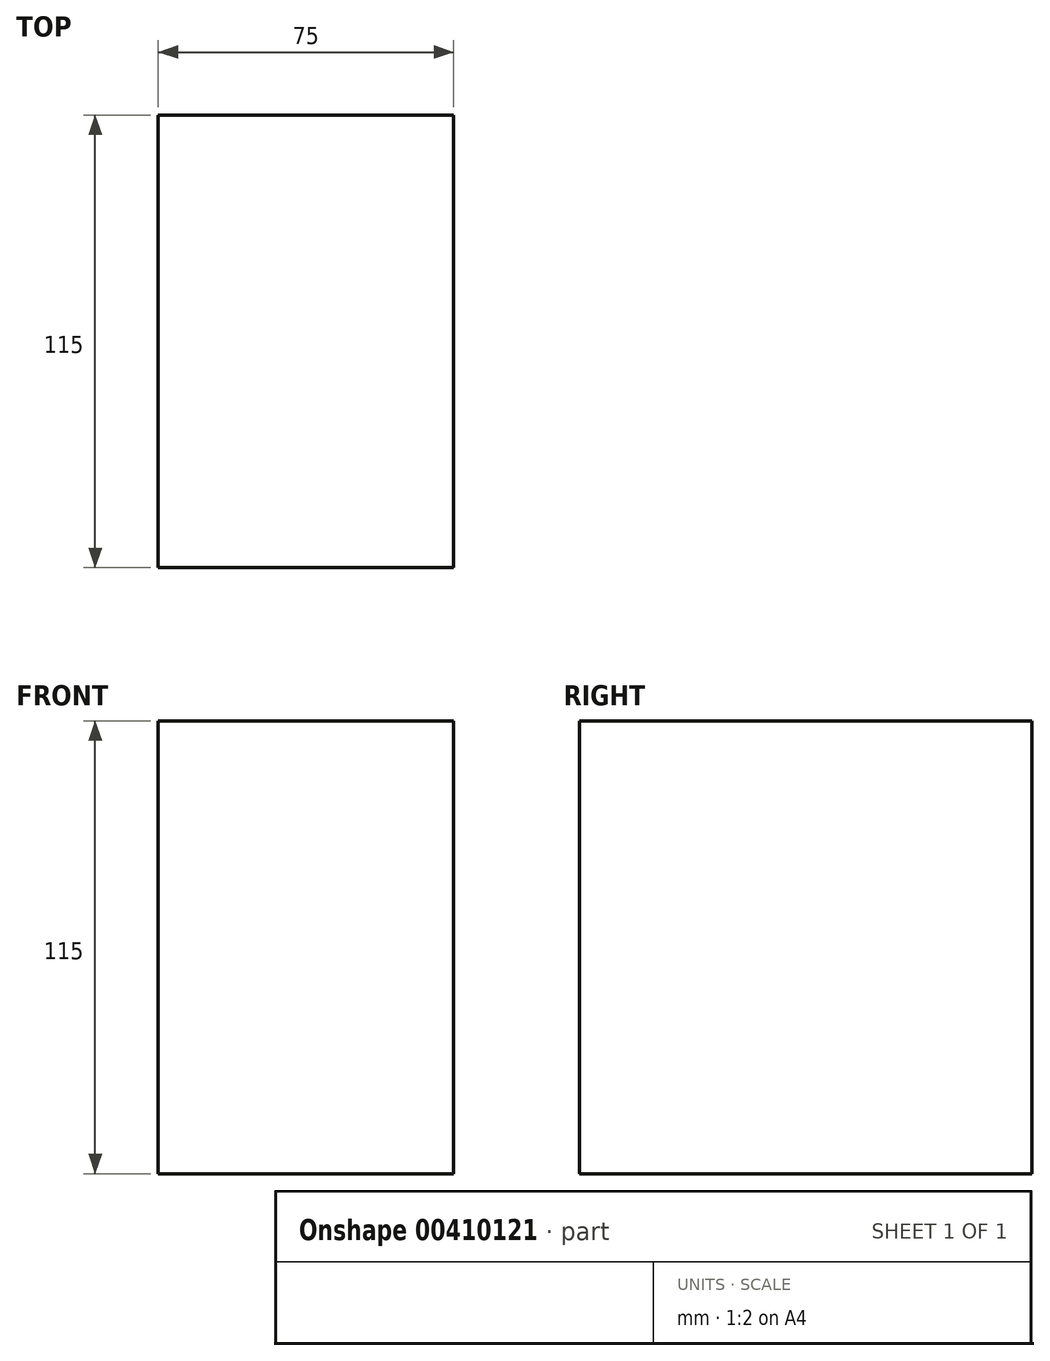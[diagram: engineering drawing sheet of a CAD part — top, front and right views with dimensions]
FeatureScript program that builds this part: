
annotation { "Feature Type Name" : "Feature", "Feature Type Description" : "" }
export const myFeature = defineFeature(function(context is Context, id is Id, definition is map)
    precondition{}
    {
        {
            var Q0;
            Q0=qCreatedBy(makeId("Front.planeOp"),FACE);
            var sketch = newSketch(context, id + "F0", { "sketchPlane" : qUnion([Q0])});
            skLineSegment(sketch, "E0.bottom", {"start": v(0, 0) * mm, "end": v(75, 0) * mm});
            skLineSegment(sketch, "E0.top", {"start": v(0, 115) * mm, "end": v(75, 115) * mm});
            skLineSegment(sketch, "E0.left", {"start": v(0, 0) * mm, "end": v(0, 115) * mm});
            skLineSegment(sketch, "E0.right", {"start": v(75, 0) * mm, "end": v(75, 115) * mm});
            skSolve(sketch);
        }
        {
            var Q0;
            Q0=qSketchRegion(id+"F0",true);
            extrude(context, id + "F1", {"entities" : qUnion([Q0]), "depth" : 115 * mm});
        }
    });
